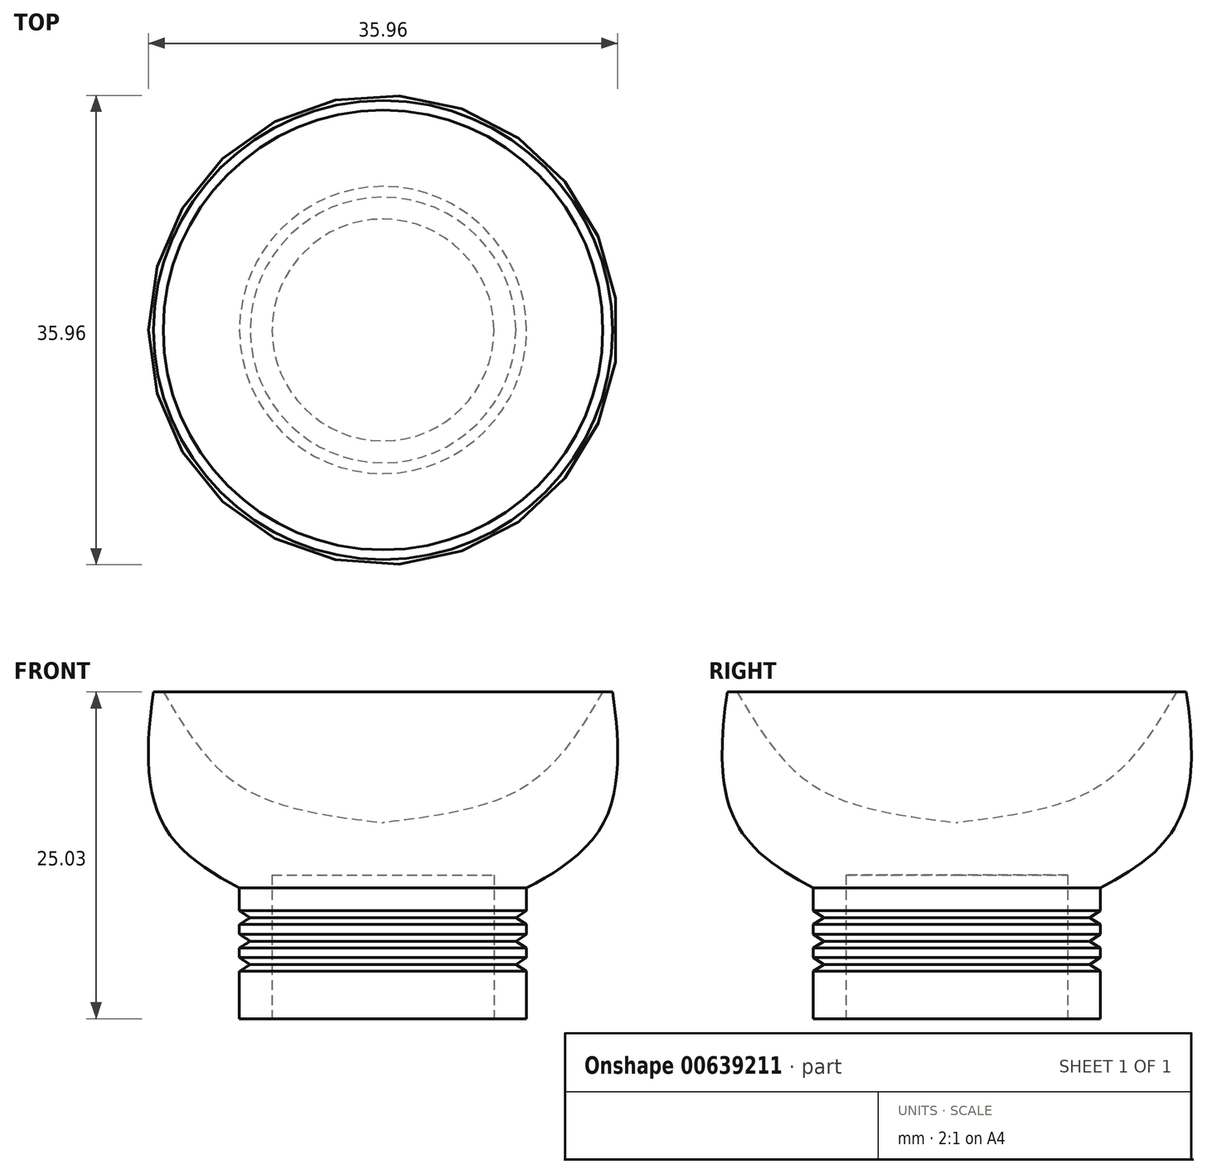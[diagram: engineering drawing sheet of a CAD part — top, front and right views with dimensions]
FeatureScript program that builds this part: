
annotation { "Feature Type Name" : "Feature", "Feature Type Description" : "" }
export const myFeature = defineFeature(function(context is Context, id is Id, definition is map)
    precondition{}
    {
        {
            var Q0;
            Q0=qCreatedBy(makeId("Front.planeOp"),FACE);
            var sketch = newSketch(context, id + "F0", { "sketchPlane" : qUnion([Q0])});
            skLineSegment(sketch, "E0", {"start": v(0, 11) * mm, "end": v(-8.5, 11) * mm});
            skLineSegment(sketch, "E1", {"start": v(-8.5, 11) * mm, "end": v(-8.5, 0) * mm});
            skLineSegment(sketch, "E2", {"start": v(-8.5, 0) * mm, "end": v(-11, 0) * mm});
            skLineSegment(sketch, "E3", {"start": v(-11, 0) * mm, "end": v(-11, 3.63) * mm});
            skLineSegment(sketch, "E4", {"start": v(-11, 3.63) * mm, "end": v(-10.18, 4.14) * mm});
            skLineSegment(sketch, "E5", {"start": v(-10.18, 4.14) * mm, "end": v(-11, 4.68) * mm});
            skLineSegment(sketch, "E6", {"start": v(-11, 4.68) * mm, "end": v(-11, 5.42) * mm});
            skLineSegment(sketch, "E7", {"start": v(-11, 5.42) * mm, "end": v(-10.18, 5.94) * mm});
            skLineSegment(sketch, "E8", {"start": v(-10.18, 5.94) * mm, "end": v(-11, 6.47) * mm});
            skLineSegment(sketch, "E9", {"start": v(-11, 6.47) * mm, "end": v(-11, 7.21) * mm});
            skLineSegment(sketch, "E10", {"start": v(-11, 7.21) * mm, "end": v(-10.18, 7.73) * mm});
            skLineSegment(sketch, "E11", {"start": v(-10.18, 7.73) * mm, "end": v(-11, 8.27) * mm});
            skLineSegment(sketch, "E12", {"start": v(-11, 8.27) * mm, "end": v(-11, 9) * mm});
            skLineSegment(sketch, "E13", {"start": v(-11, 9) * mm, "end": v(-11, 10.01) * mm});
            skFitSpline(sketch, "E14", {"points": [v(-11, 10.01) * mm, v(-16.98, 15.17) * mm, v(-17.58, 25.03) * mm], "startDerivative": vector(-16.56, 8.68) * mm, "endDerivative": vector(3.17, 21.15) * mm});
            skLineSegment(sketch, "E15", {"start": v(-17.58, 25.03) * mm, "end": v(-16.84, 25.03) * mm});
            skFitSpline(sketch, "E16", {"points": [v(-16.84, 25.03) * mm, v(-10.94, 17.83) * mm, v(0, 15.01) * mm], "startDerivative": vector(10.38, -17.46) * mm, "endDerivative": vector(23.06, -2.82) * mm});
            skLineSegment(sketch, "E17", {"start": v(0, 15.01) * mm, "end": v(0, 11) * mm});
            skSolve(sketch);
        }
        {
            var Q0;
            Q0=sQuery(id+"F0.wireOp",EDGE,"E15");
            var Q1;
            Q1=sQuery(id+"F0.wireOp",EDGE,"E16");
            var Q2;
            Q2=sQuery(id+"F0.wireOp",EDGE,"E0");
            var Q3;
            Q3=sQuery(id+"F0.wireOp",EDGE,"E14");
            var Q4;
            Q4=sQuery(id+"F0.wireOp",EDGE,"E1");
            var Q5;
            Q5=sQuery(id+"F0.wireOp",EDGE,"E13");
            var Q6;
            Q6=sQuery(id+"F0.wireOp",EDGE,"E12");
            var Q7;
            Q7=sQuery(id+"F0.wireOp",EDGE,"E11");
            var Q8;
            Q8=sQuery(id+"F0.wireOp",EDGE,"E10");
            var Q9;
            Q9=sQuery(id+"F0.wireOp",EDGE,"E9");
            var Q10;
            Q10=sQuery(id+"F0.wireOp",EDGE,"E8");
            var Q11;
            Q11=sQuery(id+"F0.wireOp",EDGE,"E7");
            var Q12;
            Q12=sQuery(id+"F0.wireOp",EDGE,"E6");
            var Q13;
            Q13=sQuery(id+"F0.wireOp",EDGE,"E5");
            var Q14;
            Q14=sQuery(id+"F0.wireOp",EDGE,"E4");
            var Q15;
            Q15=sQuery(id+"F0.wireOp",EDGE,"E3");
            var Q16;
            Q16=sQuery(id+"F0.wireOp",EDGE,"E2");
            var Q17;
            Q17=sQuery(id+"F0.wireOp",EDGE,"E17");
            revolve(context, id + "F1", {"bodyType" : ToolBodyType.SURFACE, "surfaceEntities" : qUnion([Q0, Q1, Q2, Q3, Q4, Q5, Q6, Q7, Q8, Q9, Q10, Q11, Q12, Q13, Q14, Q15, Q16]), "axis" : qUnion([Q17]), "revolveType" : RevolveType.FULL});
        }
    });
